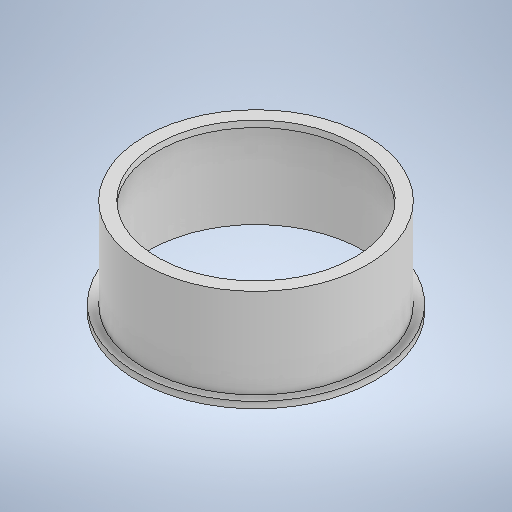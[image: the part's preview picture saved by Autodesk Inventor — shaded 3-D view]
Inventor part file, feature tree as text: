
AUTODESK INVENTOR PART (.ipt)
format: ipt  version: 2025.2 (Build 292293000, 293)  size: 326,656 bytes
history: native  units: in
note: dims shown in document units (in); Inventor stores cm internally (conversion verified against a paired STEP export)
features: other x12, sketch x9, extrude x6, plane x1
ambient origin geometry x8: Origin, YZ Plane, XZ Plane, XY Plane, X Axis, Y Axis, Z Axis, Center Point
bodies: Solid1 (feature_tree)
feature tree (28):
  other  "Table"
  other  "C .Replace - 01"
  other  "C .Replace - 02"
  other  "C .Replace - 03"
  other  "C .Replace - 04"
  other  "C .Replace - 05"
  other  "C .Replace - 06"
  other  "C .Replace - 07"
  other  "C .Replace - 08"
  other  "C .Replace - 09"
  other  "C .Replace - 10"
  other  "C .Replace - Face"
  sketch  "Sketch1"  dims[d5=0.0in d7=0.0in]
  extrude  "Extrusion1"  TaperAngle=0.0deg  [1 undecoded]
  extrude  "Extrusion2"  Depth=10.0394in
  sketch  "Sketch2"  dims[d28=0.1969in d29=3.937in d31=360.0deg]
  extrude  "Extrusion7"  Depth=3.937in TaperAngle=360.0deg
  plane  "Work Plane2"
  extrude  "Extrusion8"  Depth=0.3937in
  extrude  "Extrusion30"  Depth=0.2165in
  sketch  "Sketch25"  dims[d240=2.3622in d242=360.0deg]
  extrude  "Extrusion31"  Depth=0.3937in TaperAngle=0.0deg
  sketch  "Sketch3"  dims[d33=0.3937in d34=0.0in d52=4.5276in]
  sketch  "Sketch Circular Pattern1"  dims[d18=0.0in d27=10.0394in]
  sketch  "Sketch24"  dims[d239=0.2559in]
  sketch  "Sketch Circular Pattern4"  dims[d230=4.0157in d231=0.2165in]
  sketch  "Sketch26"  dims[d244=0.1969in d245=0.0in d113=0.0197in d114=0.0344in d115=0.0197in d116=0.0344in d167=0.0197in d168=0.0344in d169=0.0197in d170=0.0344in d215=0.0197in d216=0.0344in d217=0.0197in d218=0.0344in d219=0.0in d220=0.0in]
  sketch  "Sketch Circular Pattern5"  dims[d232=2.3622in d234=360.0deg d236=0.3937in d237=0.0in]
note: 1 required parameter value undecoded (feature->parameter linkage not recoverable at this tier; creation-order binding heuristic only, values carry confidence <= 0.55)
